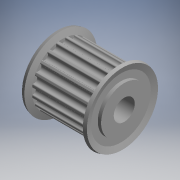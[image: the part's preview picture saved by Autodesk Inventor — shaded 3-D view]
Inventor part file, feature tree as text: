
AUTODESK INVENTOR PART (.ipt)
format: ipt  version: 2017.3 (Build 213256000, 256)  size: 242,688 bytes
history: native  units: mm (DEFAULTED — no unit token found)
features: revolve x1, extrude x1, pattern_circular x1, hole x1, sketch x1
ambient origin geometry x8: Origin, YZ Plane, XZ Plane, XY Plane, X Axis, Y Axis, Z Axis, Center Point
bodies: Solid1 (feature_tree)
feature tree (5):
  revolve  "Revolution1"  [1 undecoded]
  extrude  "Extrusion1"  Depth=20.7mm
  pattern_circular  "Circular Pattern1"  [2 undecoded]
  hole  "Hole1"  [1 undecoded]
  sketch  "Sketch3"  dims[d0=360.0deg d1=16.7mm d2=0.0mm d3=200.0mm d4=3.141593mm d6=6.35mm d7=6.0mm d8=4.0mm d9=2.0mm d10=90.0deg d11=20.7mm d12=0.0mm]
note: 4 required parameter values undecoded (feature->parameter linkage not recoverable at this tier; creation-order binding heuristic only, values carry confidence <= 0.55)